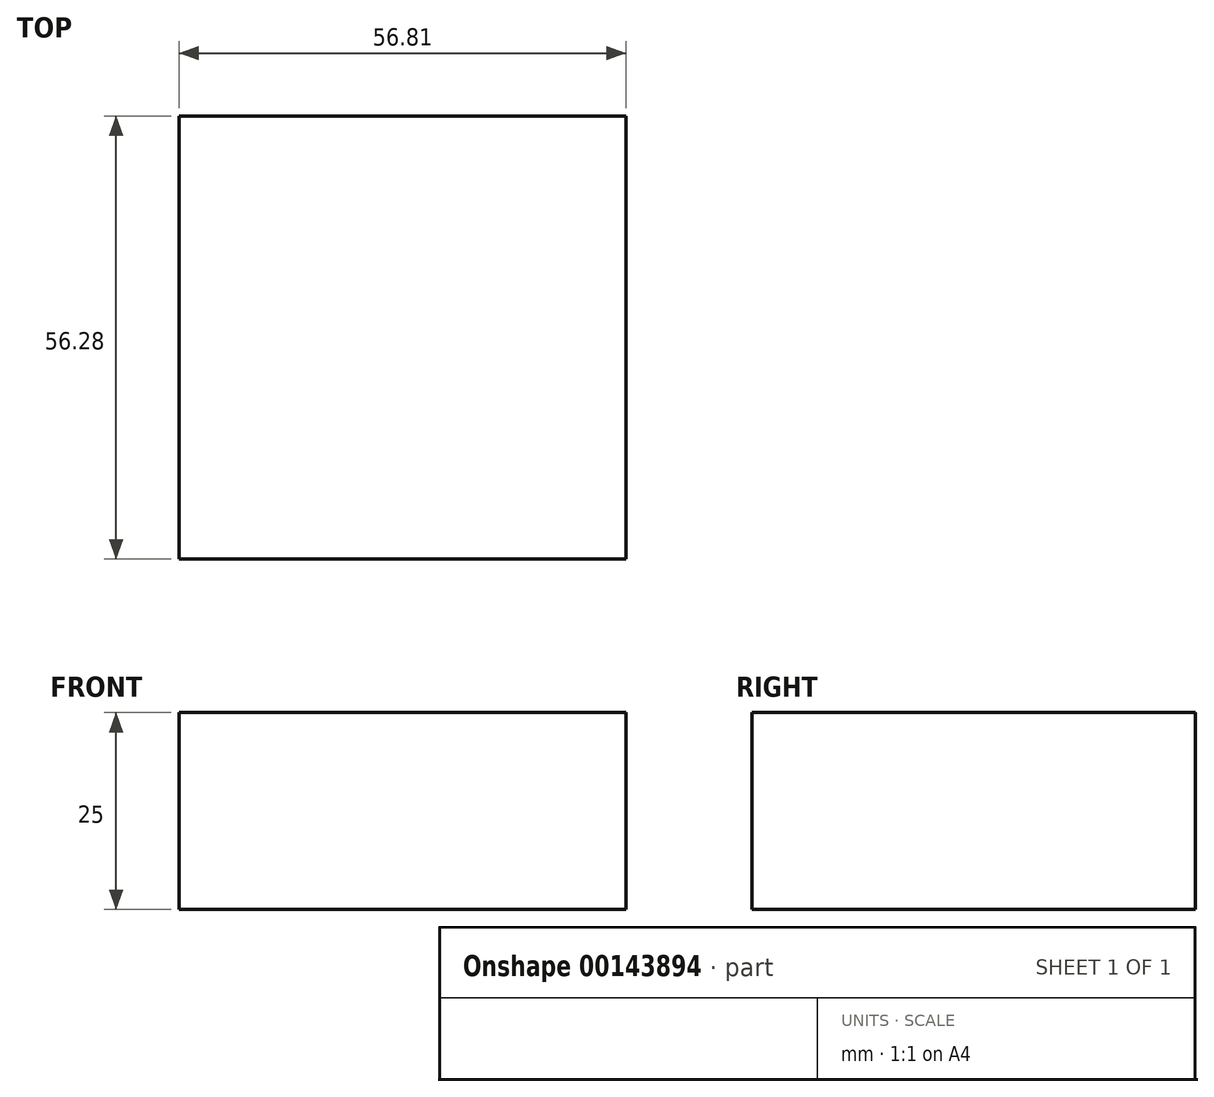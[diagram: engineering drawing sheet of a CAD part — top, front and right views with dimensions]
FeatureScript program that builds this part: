
annotation { "Feature Type Name" : "Feature", "Feature Type Description" : "" }
export const myFeature = defineFeature(function(context is Context, id is Id, definition is map)
    precondition{}
    {
        {
            var Q0;
            Q0=qCreatedBy(makeId("Top.planeOp"),FACE);
            var sketch = newSketch(context, id + "F0", { "sketchPlane" : qUnion([Q0])});
            skLineSegment(sketch, "E0.bottom", {"start": v(0, 0) * mm, "end": v(-56.8, 0) * mm});
            skLineSegment(sketch, "E0.top", {"start": v(0, 56.28) * mm, "end": v(-56.8, 56.28) * mm});
            skLineSegment(sketch, "E0.left", {"start": v(0, 0) * mm, "end": v(0, 56.28) * mm});
            skLineSegment(sketch, "E0.right", {"start": v(-56.8, 0) * mm, "end": v(-56.8, 56.28) * mm});
            skSolve(sketch);
        }
        {
            var Q0;
            Q0 = qSketchRegion(id + "F0", true);
            extrude(context, id + "F1", {"entities" : qUnion([Q0]), "oppositeDirection" : true, "depth" : 25 * mm});
        }
    });
